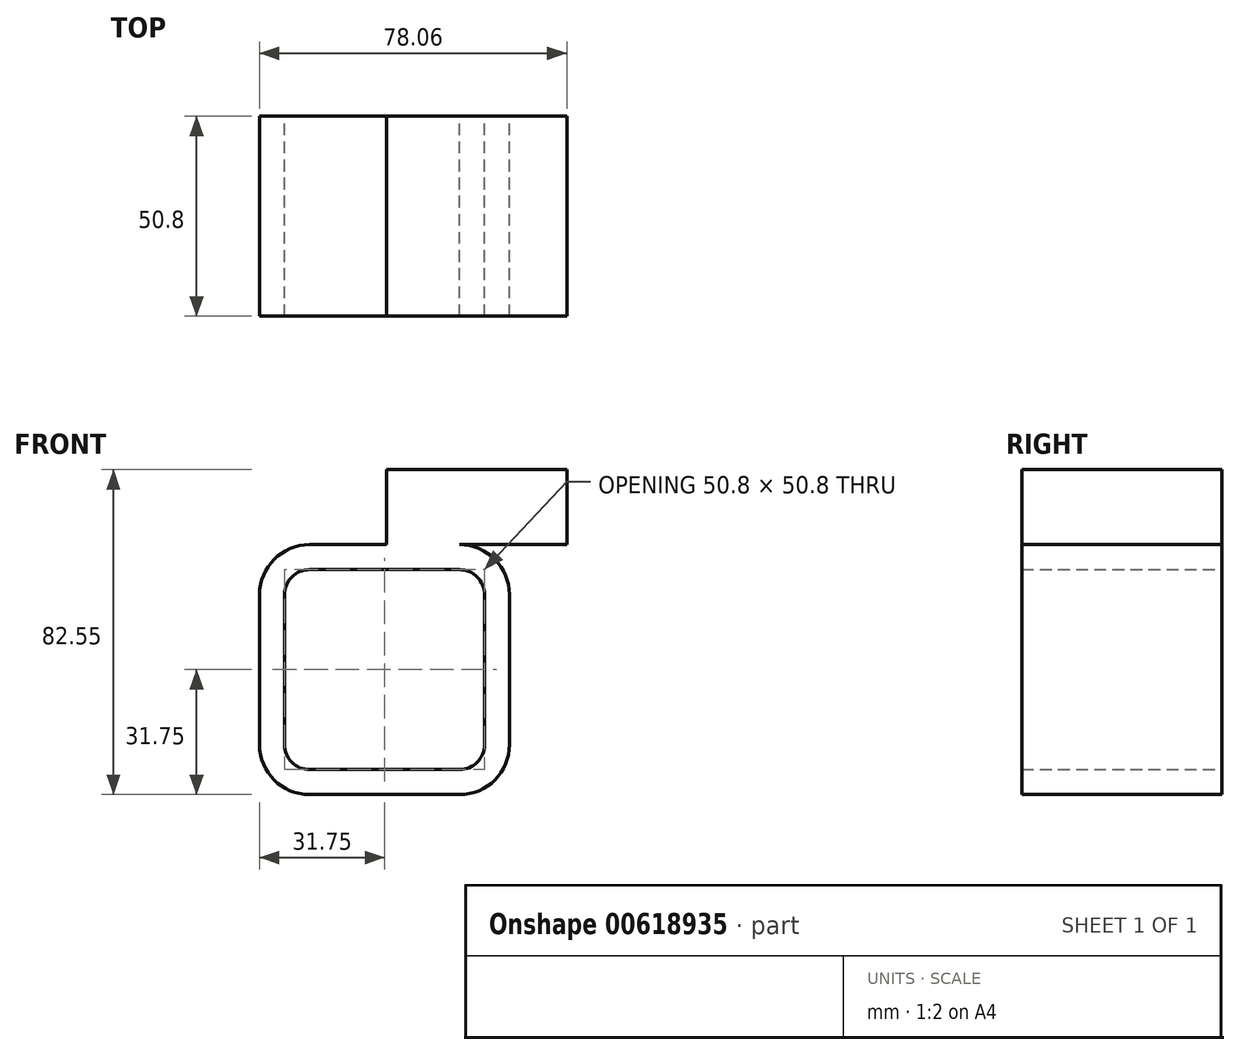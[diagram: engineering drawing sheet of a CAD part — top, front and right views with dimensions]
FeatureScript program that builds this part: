
annotation { "Feature Type Name" : "Feature", "Feature Type Description" : "" }
export const myFeature = defineFeature(function(context is Context, id is Id, definition is map)
    precondition{}
    {
        {
            var Q0;
            Q0=qCreatedBy(makeId("Front.planeOp"),FACE);
            var sketch = newSketch(context, id + "F0", { "sketchPlane" : qUnion([Q0])});
            skLineSegment(sketch, "E0.bottom", {"start": v(19.05, 31.75) * mm, "end": v(-19.05, 31.75) * mm});
            skLineSegment(sketch, "E0.top", {"start": v(19.05, -31.75) * mm, "end": v(-19.05, -31.75) * mm});
            skLineSegment(sketch, "E0.left", {"start": v(31.75, 19.05) * mm, "end": v(31.75, -19.05) * mm});
            skLineSegment(sketch, "E0.right", {"start": v(-31.75, 19.05) * mm, "end": v(-31.75, -19.05) * mm});
            skPoint(sketch, "E0.middle", {"position": v(0, 0) * mm});
            skPoint(sketch, "E1.visualSharp", {"position": v(31.75, 31.75) * mm});
            skArc(sketch, "E1.filletArc", {"start": v(31.75, 19.05) * mm, "mid": v(28.03, 28.03) * mm, "end": v(19.05, 31.75) * mm});
            skPoint(sketch, "E2.visualSharp", {"position": v(31.75, -31.75) * mm});
            skArc(sketch, "E2.filletArc", {"start": v(19.05, -31.75) * mm, "mid": v(28.03, -28.03) * mm, "end": v(31.75, -19.05) * mm});
            skPoint(sketch, "E3.visualSharp", {"position": v(-31.75, -31.75) * mm});
            skArc(sketch, "E3.filletArc", {"start": v(-31.75, -19.05) * mm, "mid": v(-28.03, -28.03) * mm, "end": v(-19.05, -31.75) * mm});
            skPoint(sketch, "E4.visualSharp", {"position": v(-31.75, 31.75) * mm});
            skArc(sketch, "E4.filletArc", {"start": v(-19.05, 31.75) * mm, "mid": v(-28.03, 28.03) * mm, "end": v(-31.75, 19.05) * mm});
            skArc(sketch, "E5.0", {"start": v(25.4, 19.05) * mm, "mid": v(23.54, 23.54) * mm, "end": v(19.05, 25.4) * mm});
            skLineSegment(sketch, "E5.1", {"start": v(25.4, 19.05) * mm, "end": v(25.4, -19.05) * mm});
            skLineSegment(sketch, "E5.2", {"start": v(19.05, 25.4) * mm, "end": v(-19.05, 25.4) * mm});
            skArc(sketch, "E5.3", {"start": v(19.05, -25.4) * mm, "mid": v(23.54, -23.54) * mm, "end": v(25.4, -19.05) * mm});
            skArc(sketch, "E5.4", {"start": v(-19.05, 25.4) * mm, "mid": v(-23.54, 23.54) * mm, "end": v(-25.4, 19.05) * mm});
            skLineSegment(sketch, "E5.5", {"start": v(-25.4, 19.05) * mm, "end": v(-25.4, -19.05) * mm});
            skArc(sketch, "E5.6", {"start": v(-25.4, -19.05) * mm, "mid": v(-23.54, -23.54) * mm, "end": v(-19.05, -25.4) * mm});
            skLineSegment(sketch, "E5.7", {"start": v(19.05, -25.4) * mm, "end": v(-19.05, -25.4) * mm});
            skSolve(sketch);
        }
        {
            var Q0;
            Q0=qCreatedBy(makeId("Right.planeOp"),FACE);
            var sketch = newSketch(context, id + "F1", { "sketchPlane" : qUnion([Q0])});
            skSolve(sketch);
        }
        {
            var Q0;
            Q0 = qSketchRegion(id + "F1", true);
            var Q1;
            Q1=makeQuery(id+"F0.imprint","IMPRINT",FACE,{"disambiguationData":[TD([[makeQuery(id+"F0.imprint","IMPRINT",EDGE,{"derivedFrom":sQuery(id+"F0.wireOp",EDGE,"E0.bottom")}),1.0]])]});
            extrude(context, id + "F2", {"entities" : qUnion([Q0, Q1]), "depth" : 50.8 * mm, "offsetDistance" : 25.4 * mm});
        }
        {
            var Q0;
            Q0=qCreatedBy(makeId("Front.planeOp"),FACE);
            var sketch = newSketch(context, id + "F3", { "sketchPlane" : qUnion([Q0])});
            skLineSegment(sketch, "E6.bottom", {"start": v(0.5, 31.75) * mm, "end": v(46.31, 31.75) * mm});
            skLineSegment(sketch, "E6.top", {"start": v(0.5, 50.8) * mm, "end": v(46.31, 50.8) * mm});
            skLineSegment(sketch, "E6.left", {"start": v(0.5, 31.75) * mm, "end": v(0.5, 50.8) * mm});
            skLineSegment(sketch, "E6.right", {"start": v(46.31, 31.75) * mm, "end": v(46.31, 50.8) * mm});
            skSolve(sketch);
        }
        {
            var Q0;
            Q0 = qSketchRegion(id + "F3", true);
            extrude(context, id + "F4", {"entities" : qUnion([Q0]), "operationType" : NewBodyOperationType.ADD, "depth" : 50.8 * mm, "offsetDistance" : 25.4 * mm});
        }
    });
